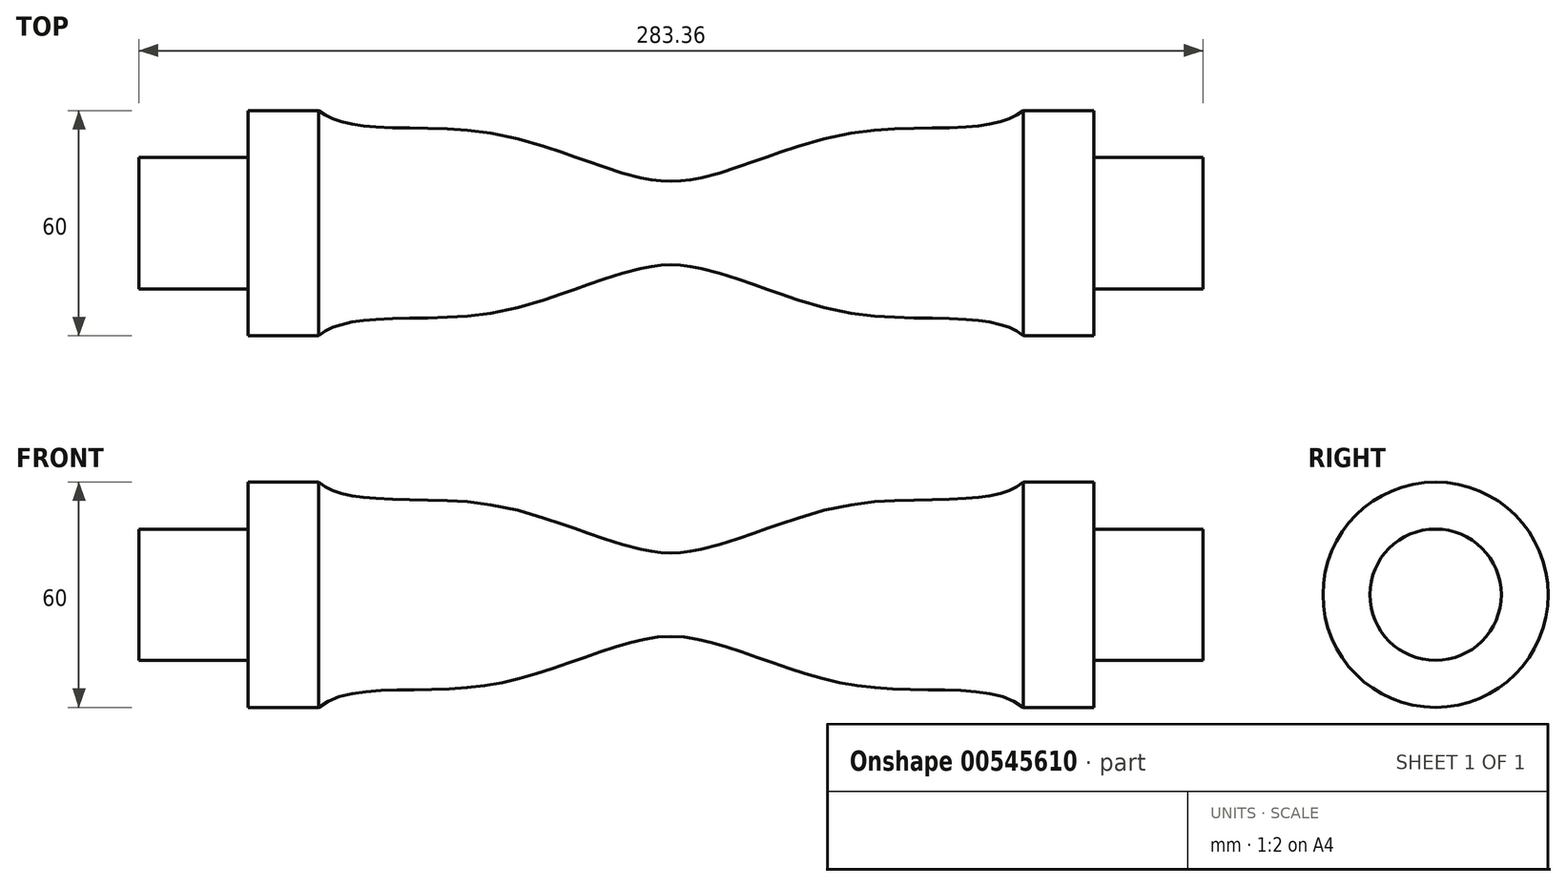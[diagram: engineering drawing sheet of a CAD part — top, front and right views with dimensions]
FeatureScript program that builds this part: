
annotation { "Feature Type Name" : "Feature", "Feature Type Description" : "" }
export const myFeature = defineFeature(function(context is Context, id is Id, definition is map)
    precondition{}
    {
        {
            var Q0;
            Q0=qCreatedBy(makeId("Front.planeOp"),FACE);
            var sketch = newSketch(context, id + "F0", { "sketchPlane" : qUnion([Q0])});
            skLineSegment(sketch, "E0", {"start": v(93.9, 30) * mm, "end": v(112.68, 30) * mm});
            skLineSegment(sketch, "E1", {"start": v(112.68, 30) * mm, "end": v(112.68, 17.5) * mm});
            skLineSegment(sketch, "E2", {"start": v(112.68, 17.5) * mm, "end": v(141.68, 17.5) * mm});
            skLineSegment(sketch, "E3", {"start": v(141.68, 17.5) * mm, "end": v(141.68, 0) * mm});
            skLineSegment(sketch, "E4", {"start": v(141.68, 0) * mm, "end": v(0, 0) * mm});
            skLineSegment(sketch, "E5", {"start": v(0, 0) * mm, "end": v(0, 11.1) * mm});
            skFitSpline(sketch, "E6", {"points": [v(0, 11.1) * mm, v(48.53, 24.06) * mm, v(93.9, 30) * mm], "startDerivative": vector(79.52, 0.21) * mm, "endDerivative": vector(52.91, 42.91) * mm});
            skSolve(sketch);
        }
        {
            var Q0;
            {var subQ8=sQuery(id+"F0.wireOp",EDGE,"E0");Q0=makeQuery(id+"F0.imprint","IMPRINT",FACE,{"disambiguationData":[TD([[makeQuery(id+"F0.imprint","IMPRINT",EDGE,{"derivedFrom":subQ8}),-1.0]])]});}
            var Q1;
            Q1=sQuery(id+"F0.wireOp",EDGE,"E4");
            revolve(context, id + "F1", {"entities" : qUnion([Q0]), "axis" : qUnion([Q1]), "revolveType" : RevolveType.FULL});
        }
        {
            var Q0;
            Q0=makeQuery(id+"F1.opRevolve","SWEPT_BODY",BODY,{"disambiguationData":[OSD([sQuery(id+"F0.wireOp",EDGE,"E0"),sQuery(id+"F0.wireOp",EDGE,"E1"),sQuery(id+"F0.wireOp",EDGE,"E2"),sQuery(id+"F0.wireOp",EDGE,"E3"),sQuery(id+"F0.wireOp",EDGE,"E4"),sQuery(id+"F0.wireOp",EDGE,"E5"),sQuery(id+"F0.wireOp",EDGE,"38873862-c52d-4dad-ab33-78162a61a8ad")])]});
            var Q1;
            Q1=makeQuery(id+"F1.opRevolve","SWEPT_FACE",FACE,{"disambiguationData":[OSD([sQuery(id+"F0.wireOp",EDGE,"E5")])]});
            mirror(context, id + "F2", {"operationType" : NewBodyOperationType.ADD, "entities" : qUnion([Q0]), "mirrorPlane" : qUnion([Q1])});
        }
    });
